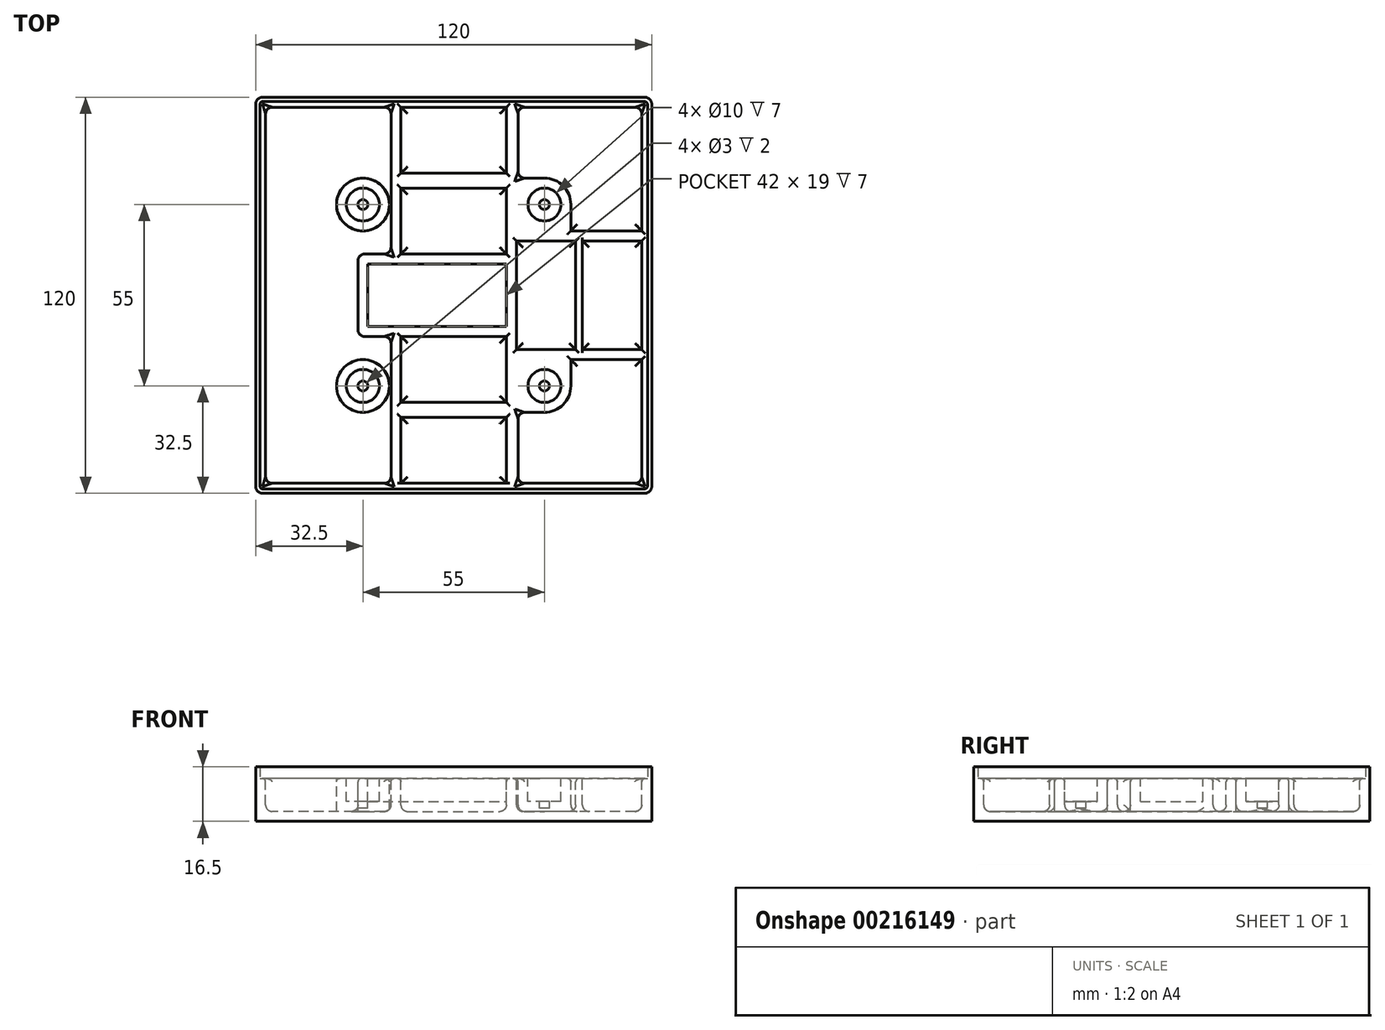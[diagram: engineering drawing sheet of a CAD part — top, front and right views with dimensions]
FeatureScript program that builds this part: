
annotation { "Feature Type Name" : "Feature", "Feature Type Description" : "" }
export const myFeature = defineFeature(function(context is Context, id is Id, definition is map)
    precondition{}
    {
        {
            var Q0;
            Q0=qCreatedBy(makeId("Top.planeOp"),FACE);
            var sketch = newSketch(context, id + "F0", { "sketchPlane" : qUnion([Q0])});
            skLineSegment(sketch, "E0.bottom", {"start": v(60, -60) * mm, "end": v(-60, -60) * mm});
            skLineSegment(sketch, "E0.top", {"start": v(60, 60) * mm, "end": v(-60, 60) * mm});
            skLineSegment(sketch, "E0.left", {"start": v(60, -60) * mm, "end": v(60, 60) * mm});
            skLineSegment(sketch, "E0.right", {"start": v(-60, -60) * mm, "end": v(-60, 60) * mm});
            skPoint(sketch, "E0.middle", {"position": v(0, 0) * mm});
            skSolve(sketch);
        }
        {
            var Q0;
            Q0=makeQuery(id+"F0.imprint","IMPRINT",FACE,{"disambiguationData":[TD([[makeQuery(id+"F0.imprint","IMPRINT",EDGE,{"derivedFrom":sQuery(id+"F0.wireOp",EDGE,"E0.bottom")}),-1.0]])]});
            extrude(context, id + "F1", {"entities" : qUnion([Q0]), "depth" : 13 * mm});
        }
        {
            var Q0;
            Q0=makeQuery(id+"F1.opExtrude","CAP_FACE",FACE,{"disambiguationData":[OSD([sQuery(id+"F0.wireOp",EDGE,"E0.bottom"),sQuery(id+"F0.wireOp",EDGE,"E0.top"),sQuery(id+"F0.wireOp",EDGE,"E0.left"),sQuery(id+"F0.wireOp",EDGE,"E0.right")])],"isStart":false});
            var sketch = newSketch(context, id + "F2", { "sketchPlane" : qUnion([Q0])});
            skLineSegment(sketch, "E1.bottom", {"start": v(16, -9.5) * mm, "end": v(-16, -9.5) * mm});
            skLineSegment(sketch, "E1.top", {"start": v(16, 9.5) * mm, "end": v(-16, 9.5) * mm});
            skLineSegment(sketch, "E1.left", {"start": v(16, -9.5) * mm, "end": v(16, 9.5) * mm});
            skLineSegment(sketch, "E1.right", {"start": v(-16, -9.5) * mm, "end": v(-16, 9.5) * mm});
            skPoint(sketch, "E1.middle", {"position": v(0, 0) * mm});
            skLineSegment(sketch, "E2", {"start": v(-16, 9.5) * mm, "end": v(-26, 9.5) * mm});
            skLineSegment(sketch, "E3", {"start": v(-26, 9.5) * mm, "end": v(-26, -9.5) * mm});
            skLineSegment(sketch, "E4", {"start": v(-26, -9.5) * mm, "end": v(-16, -9.5) * mm});
            skCircle(sketch, "E5", {"center": v(-27.5, 27.5) * mm, "radius": 5 * mm});
            skCircle(sketch, "E6", {"center": v(-27.5, -27.5) * mm, "radius": 5 * mm});
            skCircle(sketch, "E7", {"center": v(27.5, -27.5) * mm, "radius": 5 * mm});
            skCircle(sketch, "E8", {"center": v(27.5, 27.5) * mm, "radius": 5 * mm});
            skCircle(sketch, "E9", {"center": v(-27.5, 27.5) * mm, "radius": 1.5 * mm});
            skCircle(sketch, "E10", {"center": v(-27.5, -27.5) * mm, "radius": 1.5 * mm});
            skCircle(sketch, "E11", {"center": v(27.5, -27.5) * mm, "radius": 1.5 * mm});
            skCircle(sketch, "E12", {"center": v(27.5, 27.5) * mm, "radius": 1.5 * mm});
            skCircle(sketch, "E13.0", {"center": v(-27.5, 27.5) * mm, "radius": 8 * mm});
            skCircle(sketch, "E14.0", {"center": v(27.5, 27.5) * mm, "radius": 8 * mm});
            skCircle(sketch, "E15.0", {"center": v(27.5, -27.5) * mm, "radius": 8 * mm});
            skCircle(sketch, "E16.0", {"center": v(-27.5, -27.5) * mm, "radius": 8 * mm});
            skLineSegment(sketch, "E17.0", {"start": v(19, -12.5) * mm, "end": v(19, 12.5) * mm});
            skLineSegment(sketch, "E17.1", {"start": v(-29, -12.5) * mm, "end": v(-16, -12.5) * mm});
            skLineSegment(sketch, "E17.2", {"start": v(-29, 12.5) * mm, "end": v(-29, -12.5) * mm});
            skLineSegment(sketch, "E17.3", {"start": v(19, -12.5) * mm, "end": v(-16, -12.5) * mm});
            skLineSegment(sketch, "E17.4", {"start": v(-16, 12.5) * mm, "end": v(-29, 12.5) * mm});
            skLineSegment(sketch, "E17.5", {"start": v(19, 12.5) * mm, "end": v(-16, 12.5) * mm});
            skLineSegment(sketch, "E18.0", {"start": v(-57, -57) * mm, "end": v(-57, 57) * mm});
            skLineSegment(sketch, "E18.1", {"start": v(57, -57) * mm, "end": v(-57, -57) * mm});
            skLineSegment(sketch, "E18.2", {"start": v(57, -57) * mm, "end": v(57, 57) * mm});
            skLineSegment(sketch, "E18.3", {"start": v(57, 57) * mm, "end": v(-57, 57) * mm});
            skLineSegment(sketch, "E19", {"start": v(-16, 12.5) * mm, "end": v(-16, 57) * mm});
            skLineSegment(sketch, "E20", {"start": v(16, 12.5) * mm, "end": v(16, 57) * mm});
            skLineSegment(sketch, "E21", {"start": v(-16, 32.5) * mm, "end": v(16, 32.5) * mm});
            skLineSegment(sketch, "E22", {"start": v(19, 12.5) * mm, "end": v(19, 16.5) * mm});
            skLineSegment(sketch, "E23", {"start": v(19, 16.5) * mm, "end": v(37, 16.5) * mm});
            skLineSegment(sketch, "E24", {"start": v(37, 16.5) * mm, "end": v(37, -16.5) * mm});
            skLineSegment(sketch, "E25", {"start": v(37, -16.5) * mm, "end": v(19, -16.5) * mm});
            skLineSegment(sketch, "E26", {"start": v(19, -16.5) * mm, "end": v(19, -12.5) * mm});
            skLineSegment(sketch, "E27", {"start": v(-16, -12.5) * mm, "end": v(-16, -57) * mm});
            skLineSegment(sketch, "E28", {"start": v(16, -12.5) * mm, "end": v(16, -57) * mm});
            skLineSegment(sketch, "E29", {"start": v(-16, -32.5) * mm, "end": v(16, -32.5) * mm});
            skLineSegment(sketch, "E30", {"start": v(-19, 57) * mm, "end": v(-19, 12.5) * mm});
            skLineSegment(sketch, "E31", {"start": v(-19, -12.5) * mm, "end": v(-19, -57) * mm});
            skLineSegment(sketch, "E32", {"start": v(-16, -37) * mm, "end": v(16, -37) * mm});
            skLineSegment(sketch, "E33", {"start": v(-16, 37) * mm, "end": v(16, 37) * mm});
            skLineSegment(sketch, "E34", {"start": v(19.5, 57) * mm, "end": v(19.5, 27.5) * mm});
            skLineSegment(sketch, "E35", {"start": v(19.5, -57) * mm, "end": v(19.5, -27.5) * mm});
            skLineSegment(sketch, "E36", {"start": v(19.5, -35.5) * mm, "end": v(27.5, -35.5) * mm});
            skLineSegment(sketch, "E37", {"start": v(19.5, 35.5) * mm, "end": v(27.5, 35.5) * mm});
            skLineSegment(sketch, "E38", {"start": v(57, 19.5) * mm, "end": v(27.5, 19.5) * mm});
            skLineSegment(sketch, "E39", {"start": v(35.5, 19.5) * mm, "end": v(35.5, 27.5) * mm});
            skLineSegment(sketch, "E40", {"start": v(57, -19.5) * mm, "end": v(27.5, -19.5) * mm});
            skLineSegment(sketch, "E41", {"start": v(35.5, -19.5) * mm, "end": v(35.5, -27.5) * mm});
            skLineSegment(sketch, "E42", {"start": v(57, 16.5) * mm, "end": v(39, 16.5) * mm});
            skLineSegment(sketch, "E43", {"start": v(39, 16.5) * mm, "end": v(39, -16.5) * mm});
            skLineSegment(sketch, "E44", {"start": v(39, -16.5) * mm, "end": v(57, -16.5) * mm});
            skSolve(sketch);
        }
        {
            var Q0;
            Q0=makeQuery(id+"F2.imprint","IMPRINT",FACE,{"disambiguationData":[TD([[makeQuery(id+"F2.imprint","IMPRINT",EDGE,{"derivedFrom":sQuery(id+"F2.wireOp",EDGE,"E1.right")}),1.0]])]});
            var Q1;
            Q1=makeQuery(id+"F2.imprint","IMPRINT",FACE,{"disambiguationData":[TD([[makeQuery(id+"F2.imprint","IMPRINT",EDGE,{"derivedFrom":sQuery(id+"F2.wireOp",EDGE,"E1.bottom")}),-1.0]])]});
            extrude(context, id + "F3", {"entities" : qUnion([Q0, Q1]), "operationType" : NewBodyOperationType.REMOVE, "oppositeDirection" : true, "depth" : 7 * mm});
        }
        {
            var Q0;
            Q0=makeQuery(id+"F2.imprint","IMPRINT",FACE,{"disambiguationData":[TD([[makeQuery(id+"F2.imprint","IMPRINT",EDGE,{"derivedFrom":sQuery(id+"F2.wireOp",EDGE,"E5")}),1.0]])]});
            var Q1;
            Q1=makeQuery(id+"F2.imprint","IMPRINT",FACE,{"disambiguationData":[TD([[makeQuery(id+"F2.imprint","IMPRINT",EDGE,{"derivedFrom":sQuery(id+"F2.wireOp",EDGE,"E6")}),1.0]])]});
            var Q2;
            Q2=makeQuery(id+"F2.imprint","IMPRINT",FACE,{"disambiguationData":[TD([[makeQuery(id+"F2.imprint","IMPRINT",EDGE,{"derivedFrom":sQuery(id+"F2.wireOp",EDGE,"E7")}),1.0]])]});
            var Q3;
            Q3=makeQuery(id+"F2.imprint","IMPRINT",FACE,{"disambiguationData":[TD([[makeQuery(id+"F2.imprint","IMPRINT",EDGE,{"derivedFrom":sQuery(id+"F2.wireOp",EDGE,"E8")}),1.0]])]});
            extrude(context, id + "F4", {"entities" : qUnion([Q0, Q1, Q2, Q3]), "operationType" : NewBodyOperationType.REMOVE, "oppositeDirection" : true, "depth" : 7 * mm});
        }
        {
            var Q0;
            Q0=makeQuery(id+"F2.imprint","IMPRINT",FACE,{"disambiguationData":[TD([[makeQuery(id+"F2.imprint","IMPRINT",EDGE,{"derivedFrom":sQuery(id+"F2.wireOp",EDGE,"E9")}),1.0]])]});
            var Q1;
            Q1=makeQuery(id+"F2.imprint","IMPRINT",FACE,{"disambiguationData":[TD([[makeQuery(id+"F2.imprint","IMPRINT",EDGE,{"derivedFrom":sQuery(id+"F2.wireOp",EDGE,"E12")}),1.0]])]});
            var Q2;
            Q2=makeQuery(id+"F2.imprint","IMPRINT",FACE,{"disambiguationData":[TD([[makeQuery(id+"F2.imprint","IMPRINT",EDGE,{"derivedFrom":sQuery(id+"F2.wireOp",EDGE,"E11")}),1.0]])]});
            var Q3;
            Q3=makeQuery(id+"F2.imprint","IMPRINT",FACE,{"disambiguationData":[TD([[makeQuery(id+"F2.imprint","IMPRINT",EDGE,{"derivedFrom":sQuery(id+"F2.wireOp",EDGE,"E10")}),1.0]])]});
            extrude(context, id + "F5", {"entities" : qUnion([Q0, Q1, Q2, Q3]), "operationType" : NewBodyOperationType.REMOVE, "oppositeDirection" : true, "depth" : 9 * mm});
        }
        {
            var Q0;
            {var subQ5=sQuery(id+"F2.wireOp",EDGE,"FMWFYpV9-Ew7e-ZcVp-ZZrZ-oKRKmoRq2qlx");Q0=makeQuery(id+"F2.imprint","IMPRINT",FACE,{"disambiguationData":[TD([[makeQuery(id+"F2.imprint","IMPRINT",EDGE,{"derivedFrom":subQ5}),1.0]])]});}
            var Q1;
            {var subQ5=sQuery(id+"F2.wireOp",EDGE,"E21");Q1=makeQuery(id+"F2.imprint","IMPRINT",FACE,{"disambiguationData":[TD([[makeQuery(id+"F2.imprint","IMPRINT",EDGE,{"derivedFrom":subQ5}),-1.0]])]});}
            var Q2;
            Q2=makeQuery(id+"F2.imprint","IMPRINT",FACE,{"disambiguationData":[TD([[makeQuery(id+"F2.imprint","IMPRINT",EDGE,{"derivedFrom":sQuery(id+"F2.wireOp",EDGE,"E13.0")}),-1.0]])]});
            var Q3;
            {var subQ5=sQuery(id+"F2.wireOp",EDGE,"E29");Q3=makeQuery(id+"F2.imprint","IMPRINT",FACE,{"disambiguationData":[TD([[makeQuery(id+"F2.imprint","IMPRINT",EDGE,{"derivedFrom":subQ5}),1.0]])]});}
            var Q4;
            {var subQ5=sQuery(id+"F2.wireOp",EDGE,"E32");Q4=makeQuery(id+"F2.imprint","IMPRINT",FACE,{"disambiguationData":[TD([[makeQuery(id+"F2.imprint","IMPRINT",EDGE,{"derivedFrom":subQ5}),-1.0]])]});}
            var Q5;
            {var subQ3=sQuery(id+"F2.wireOp",EDGE,"E36");Q5=makeQuery(id+"F2.imprint","IMPRINT",FACE,{"disambiguationData":[TD([[makeQuery(id+"F2.imprint","IMPRINT",EDGE,{"derivedFrom":subQ3}),-1.0]])]});}
            var Q6;
            Q6=makeQuery(id+"F2.imprint","IMPRINT",FACE,{"disambiguationData":[TD([[makeQuery(id+"F2.imprint","IMPRINT",EDGE,{"derivedFrom":sQuery(id+"F2.wireOp",EDGE,"E17.0")}),-1.0]])]});
            var Q7;
            {var subQ0=sQuery(id+"F2.wireOp",EDGE,"E42");Q7=makeQuery(id+"F2.imprint","IMPRINT",FACE,{"disambiguationData":[TD([[makeQuery(id+"F2.imprint","IMPRINT",EDGE,{"derivedFrom":subQ0}),1.0]])]});}
            var Q8;
            {var subQ5=sQuery(id+"F2.wireOp",EDGE,"E37");Q8=makeQuery(id+"F2.imprint","IMPRINT",FACE,{"disambiguationData":[TD([[makeQuery(id+"F2.imprint","IMPRINT",EDGE,{"derivedFrom":subQ5}),1.0]])]});}
            var Q9;
            {var subQ5=sQuery(id+"F2.wireOp",EDGE,"E33");Q9=makeQuery(id+"F2.imprint","IMPRINT",FACE,{"disambiguationData":[TD([[makeQuery(id+"F2.imprint","IMPRINT",EDGE,{"derivedFrom":subQ5}),1.0]])]});}
            extrude(context, id + "F6", {"entities" : qUnion([Q0, Q1, Q2, Q3, Q4, Q5, Q6, Q7, Q8, Q9]), "operationType" : NewBodyOperationType.REMOVE, "oppositeDirection" : true, "depth" : 10 * mm});
        }
        {
            var Q0;
            {var subQ6=sQuery(id+"F2.wireOp",EDGE,"E18.0");Q0=makeQuery(id+"F2.imprint","IMPRINT",FACE,{"disambiguationData":[TD([[makeQuery(id+"F2.imprint","IMPRINT",EDGE,{"derivedFrom":subQ6}),1.0]])]});}
            var sketch = newSketch(context, id + "F7", { "sketchPlane" : qUnion([Q0])});
            skLineSegment(sketch, "E45.0", {"start": v(58.75, 58.75) * mm, "end": v(-58.75, 58.75) * mm});
            skLineSegment(sketch, "E45.1", {"start": v(58.75, -58.75) * mm, "end": v(58.75, 58.75) * mm});
            skLineSegment(sketch, "E45.2", {"start": v(58.75, -58.75) * mm, "end": v(-58.75, -58.75) * mm});
            skLineSegment(sketch, "E45.3", {"start": v(-58.75, -58.75) * mm, "end": v(-58.75, 58.75) * mm});
            skSolve(sketch);
        }
        {
            var Q0;
            Q0=makeQuery(id+"F7.imprint","IMPRINT",FACE,{"disambiguationData":[TD([[makeQuery(id+"F7.imprint","IMPRINT",EDGE,{"derivedFrom":sQuery(id+"F7.wireOp",EDGE,"E45.0")}),-1.0]])]});
            extrude(context, id + "F8", {"entities" : qUnion([Q0]), "operationType" : NewBodyOperationType.ADD, "depth" : 3.5 * mm});
        }
        {
            var Q0;
            Q0=makeQuery(id+"F4.boolean.opBoolean","COPY",EDGE,{"derivedFrom":makeQuery(id+"F4.opExtrude","CAP_EDGE",EDGE,{"disambiguationData":[OSD([sQuery(id+"F2.wireOp",EDGE,"E5")])],"isStart":true})});
            var Q1;
            Q1=makeQuery(id+"F4.boolean.opBoolean","COPY",EDGE,{"derivedFrom":makeQuery(id+"F4.opExtrude","CAP_EDGE",EDGE,{"disambiguationData":[OSD([sQuery(id+"F2.wireOp",EDGE,"E8")])],"isStart":true})});
            var Q2;
            Q2=makeQuery(id+"F3.boolean.opBoolean","COPY",EDGE,{"derivedFrom":makeQuery(id+"F3.opExtrude","CAP_EDGE",EDGE,{"disambiguationData":[OSD([sQuery(id+"F2.wireOp",EDGE,"E1.top"),sQuery(id+"F2.wireOp",EDGE,"E2")])],"isStart":true})});
            var Q3;
            Q3=makeQuery(id+"F3.boolean.opBoolean","COPY",EDGE,{"derivedFrom":makeQuery(id+"F3.opExtrude","CAP_EDGE",EDGE,{"disambiguationData":[OSD([sQuery(id+"F2.wireOp",EDGE,"E1.left")])],"isStart":true})});
            var Q4;
            Q4=makeQuery(id+"F3.boolean.opBoolean","COPY",EDGE,{"derivedFrom":makeQuery(id+"F3.opExtrude","CAP_EDGE",EDGE,{"disambiguationData":[OSD([sQuery(id+"F2.wireOp",EDGE,"E1.bottom"),sQuery(id+"F2.wireOp",EDGE,"E4")])],"isStart":true})});
            var Q5;
            Q5=makeQuery(id+"F3.boolean.opBoolean","COPY",EDGE,{"derivedFrom":makeQuery(id+"F3.opExtrude","CAP_EDGE",EDGE,{"disambiguationData":[OSD([sQuery(id+"F2.wireOp",EDGE,"E3")])],"isStart":true})});
            var Q6;
            Q6=makeQuery(id+"F4.boolean.opBoolean","COPY",EDGE,{"derivedFrom":makeQuery(id+"F4.opExtrude","CAP_EDGE",EDGE,{"disambiguationData":[OSD([sQuery(id+"F2.wireOp",EDGE,"E6")])],"isStart":true})});
            var Q7;
            Q7=makeQuery(id+"F4.boolean.opBoolean","COPY",EDGE,{"derivedFrom":makeQuery(id+"F4.opExtrude","CAP_EDGE",EDGE,{"disambiguationData":[OSD([sQuery(id+"F2.wireOp",EDGE,"E7")])],"isStart":true})});
            var Q8;
            {var subQ0=sQuery(id+"F2.wireOp",EDGE,"E19");Q8=makeQuery(id+"F6.boolean.opBoolean","COPY",EDGE,{"derivedFrom":makeQuery(id+"F6.opExtrude","CAP_EDGE",EDGE,{"disambiguationData":[OSD([subQ0]),TDD([makeQuery(id+"F2.imprint","IMPRINT",EDGE,{"disambiguationData":[TD([[makeQuery(id+"F2.imprint","INTERSECT",VERTEX,{"derivedFrom":[subQ0,sQuery(id+"F2.wireOp",EDGE,"E21")]}),1.0]])],"derivedFrom":subQ0})])],"isStart":true})});}
            var Q9;
            Q9=makeQuery(id+"F6.boolean.opBoolean","COPY",EDGE,{"derivedFrom":makeQuery(id+"F6.opExtrude","CAP_EDGE",EDGE,{"disambiguationData":[OSD([sQuery(id+"F2.wireOp",EDGE,"E17.5")])],"isStart":true})});
            var Q10;
            Q10=makeQuery(id+"F6.boolean.opBoolean","COPY",EDGE,{"derivedFrom":makeQuery(id+"F6.opExtrude","CAP_EDGE",EDGE,{"disambiguationData":[OSD([sQuery(id+"F2.wireOp",EDGE,"E21")])],"isStart":true})});
            var Q11;
            {var subQ0=sQuery(id+"F2.wireOp",EDGE,"E19");Q11=makeQuery(id+"F6.boolean.opBoolean","COPY",EDGE,{"derivedFrom":makeQuery(id+"F6.opExtrude","CAP_EDGE",EDGE,{"disambiguationData":[OSD([subQ0]),TDD([makeQuery(id+"F2.imprint","IMPRINT",EDGE,{"disambiguationData":[TD([[makeQuery(id+"F2.imprint","INTERSECT",VERTEX,{"derivedFrom":[sQuery(id+"F2.wireOp",EDGE,"E18.3"),subQ0]}),1.0]])],"derivedFrom":subQ0})])],"isStart":true})});}
            var Q12;
            Q12=makeQuery(id+"F6.boolean.opBoolean","COPY",EDGE,{"derivedFrom":makeQuery(id+"F6.opExtrude","CAP_EDGE",EDGE,{"disambiguationData":[OSD([sQuery(id+"F2.wireOp",EDGE,"FMWFYpV9-Ew7e-ZcVp-ZZrZ-oKRKmoRq2qlx")])],"isStart":true})});
            var Q13;
            {var subQ0=sQuery(id+"F2.wireOp",EDGE,"E20");Q13=makeQuery(id+"F6.boolean.opBoolean","COPY",EDGE,{"derivedFrom":makeQuery(id+"F6.opExtrude","CAP_EDGE",EDGE,{"disambiguationData":[OSD([subQ0]),TDD([makeQuery(id+"F2.imprint","IMPRINT",EDGE,{"disambiguationData":[TD([[makeQuery(id+"F2.imprint","INTERSECT",VERTEX,{"derivedFrom":[sQuery(id+"F2.wireOp",EDGE,"E18.3"),subQ0]}),1.0]])],"derivedFrom":subQ0})])],"isStart":true})});}
            var Q14;
            Q14=makeQuery(id+"F6.boolean.opBoolean","COPY",EDGE,{"derivedFrom":makeQuery(id+"F6.opExtrude","CAP_EDGE",EDGE,{"disambiguationData":[OSD([sQuery(id+"F2.wireOp",EDGE,"E17.0"),sQuery(id+"F2.wireOp",EDGE,"E22"),sQuery(id+"F2.wireOp",EDGE,"E26")])],"isStart":true})});
            var Q15;
            Q15=makeQuery(id+"F6.boolean.opBoolean","COPY",EDGE,{"derivedFrom":makeQuery(id+"F6.opExtrude","CAP_EDGE",EDGE,{"disambiguationData":[OSD([sQuery(id+"F2.wireOp",EDGE,"E23")])],"isStart":true})});
            var Q16;
            Q16=makeQuery(id+"F6.boolean.opBoolean","COPY",EDGE,{"derivedFrom":makeQuery(id+"F6.opExtrude","CAP_EDGE",EDGE,{"disambiguationData":[OSD([sQuery(id+"F2.wireOp",EDGE,"E24")])],"isStart":true})});
            var Q17;
            Q17=makeQuery(id+"F6.boolean.opBoolean","COPY",EDGE,{"derivedFrom":makeQuery(id+"F6.opExtrude","CAP_EDGE",EDGE,{"disambiguationData":[OSD([sQuery(id+"F2.wireOp",EDGE,"E25")])],"isStart":true})});
            var Q18;
            {var subQ0=sQuery(id+"F2.wireOp",EDGE,"E28");Q18=makeQuery(id+"F6.boolean.opBoolean","COPY",EDGE,{"derivedFrom":makeQuery(id+"F6.opExtrude","CAP_EDGE",EDGE,{"disambiguationData":[OSD([subQ0]),TDD([makeQuery(id+"F2.imprint","IMPRINT",EDGE,{"disambiguationData":[TD([[makeQuery(id+"F2.imprint","INTERSECT",VERTEX,{"derivedFrom":[sQuery(id+"F2.wireOp",EDGE,"E17.3"),subQ0]}),-1.0]])],"derivedFrom":subQ0})])],"isStart":true})});}
            var Q19;
            {var subQ0=sQuery(id+"F2.wireOp",EDGE,"E28");Q19=makeQuery(id+"F6.boolean.opBoolean","COPY",EDGE,{"derivedFrom":makeQuery(id+"F6.opExtrude","CAP_EDGE",EDGE,{"disambiguationData":[OSD([subQ0]),TDD([makeQuery(id+"F2.imprint","IMPRINT",EDGE,{"disambiguationData":[TD([[makeQuery(id+"F2.imprint","INTERSECT",VERTEX,{"derivedFrom":[sQuery(id+"F2.wireOp",EDGE,"E18.1"),subQ0]}),1.0]])],"derivedFrom":subQ0})])],"isStart":true})});}
            var Q20;
            Q20=makeQuery(id+"F6.boolean.opBoolean","COPY",EDGE,{"derivedFrom":makeQuery(id+"F6.opExtrude","CAP_EDGE",EDGE,{"disambiguationData":[OSD([sQuery(id+"F2.wireOp",EDGE,"KB4tX4Ro-G294-vaRV-RxTP-gQnuyON8fFV4")])],"isStart":true})});
            var Q21;
            Q21=makeQuery(id+"F6.boolean.opBoolean","COPY",EDGE,{"derivedFrom":makeQuery(id+"F6.opExtrude","CAP_EDGE",EDGE,{"disambiguationData":[OSD([sQuery(id+"F2.wireOp",EDGE,"E29")])],"isStart":true})});
            var Q22;
            Q22=makeQuery(id+"F6.boolean.opBoolean","COPY",EDGE,{"derivedFrom":makeQuery(id+"F6.opExtrude","CAP_EDGE",EDGE,{"disambiguationData":[OSD([sQuery(id+"F2.wireOp",EDGE,"E17.3")])],"isStart":true})});
            var Q23;
            {var subQ0=sQuery(id+"F2.wireOp",EDGE,"E27");Q23=makeQuery(id+"F6.boolean.opBoolean","COPY",EDGE,{"derivedFrom":makeQuery(id+"F6.opExtrude","CAP_EDGE",EDGE,{"disambiguationData":[OSD([subQ0]),TDD([makeQuery(id+"F2.imprint","IMPRINT",EDGE,{"disambiguationData":[TD([[makeQuery(id+"F2.imprint","INTERSECT",VERTEX,{"derivedFrom":[subQ0,sQuery(id+"F2.wireOp",EDGE,"E29")]}),1.0]])],"derivedFrom":subQ0})])],"isStart":true})});}
            var Q24;
            {var subQ0=sQuery(id+"F2.wireOp",EDGE,"E27");Q24=makeQuery(id+"F6.boolean.opBoolean","COPY",EDGE,{"derivedFrom":makeQuery(id+"F6.opExtrude","CAP_EDGE",EDGE,{"disambiguationData":[OSD([subQ0]),TDD([makeQuery(id+"F2.imprint","IMPRINT",EDGE,{"disambiguationData":[TD([[makeQuery(id+"F2.imprint","INTERSECT",VERTEX,{"derivedFrom":[sQuery(id+"F2.wireOp",EDGE,"E18.1"),subQ0]}),1.0]])],"derivedFrom":subQ0})])],"isStart":true})});}
            var Q25;
            {var subQ0=sQuery(id+"F2.wireOp",EDGE,"E20");Q25=makeQuery(id+"F6.boolean.opBoolean","COPY",EDGE,{"derivedFrom":makeQuery(id+"F6.opExtrude","CAP_EDGE",EDGE,{"disambiguationData":[OSD([subQ0]),TDD([makeQuery(id+"F2.imprint","IMPRINT",EDGE,{"disambiguationData":[TD([[makeQuery(id+"F2.imprint","INTERSECT",VERTEX,{"derivedFrom":[sQuery(id+"F2.wireOp",EDGE,"E17.5"),subQ0]}),-1.0]])],"derivedFrom":subQ0})])],"isStart":true})});}
            var Q26;
            Q26=makeQuery(id+"F6.boolean.opBoolean","COPY",EDGE,{"derivedFrom":makeQuery(id+"F6.opExtrude","CAP_EDGE",EDGE,{"disambiguationData":[OSD([sQuery(id+"F2.wireOp",EDGE,"E16.0")])],"isStart":true})});
            var Q27;
            Q27=makeQuery(id+"F6.boolean.opBoolean","COPY",EDGE,{"derivedFrom":makeQuery(id+"F6.opExtrude","CAP_EDGE",EDGE,{"disambiguationData":[OSD([sQuery(id+"F2.wireOp",EDGE,"E13.0")])],"isStart":true})});
            var Q28;
            {var subQ0=sQuery(id+"F2.wireOp",EDGE,"E19");Q28=makeQuery(id+"F6.boolean.opBoolean","COPY",EDGE,{"derivedFrom":makeQuery(id+"F6.opExtrude","CAP_EDGE",EDGE,{"disambiguationData":[OSD([subQ0]),TDD([makeQuery(id+"F2.imprint","IMPRINT",EDGE,{"disambiguationData":[TD([[makeQuery(id+"F2.imprint","INTERSECT",VERTEX,{"derivedFrom":[subQ0,sQuery(id+"F2.wireOp",EDGE,"72itZujO-k5kq-emlP-LSjC-fSTvy6e93rC8")]}),1.0]])],"derivedFrom":subQ0})])],"isStart":true})});}
            var Q29;
            Q29=makeQuery(id+"F6.boolean.opBoolean","COPY",EDGE,{"derivedFrom":makeQuery(id+"F6.opExtrude","CAP_EDGE",EDGE,{"disambiguationData":[OSD([sQuery(id+"F2.wireOp",EDGE,"72itZujO-k5kq-emlP-LSjC-fSTvy6e93rC8")])],"isStart":true})});
            var Q30;
            Q30=makeQuery(id+"F6.boolean.opBoolean","COPY",EDGE,{"derivedFrom":makeQuery(id+"F6.opExtrude","CAP_EDGE",EDGE,{"disambiguationData":[OSD([sQuery(id+"F2.wireOp",EDGE,"E33")])],"isStart":true})});
            var Q31;
            {var subQ0=sQuery(id+"F2.wireOp",EDGE,"E20");Q31=makeQuery(id+"F6.boolean.opBoolean","COPY",EDGE,{"derivedFrom":makeQuery(id+"F6.opExtrude","CAP_EDGE",EDGE,{"disambiguationData":[OSD([subQ0]),TDD([makeQuery(id+"F2.imprint","IMPRINT",EDGE,{"disambiguationData":[TD([[makeQuery(id+"F2.imprint","INTERSECT",VERTEX,{"derivedFrom":[subQ0,sQuery(id+"F2.wireOp",EDGE,"72itZujO-k5kq-emlP-LSjC-fSTvy6e93rC8")]}),1.0]])],"derivedFrom":subQ0})])],"isStart":true})});}
            var Q32;
            Q32=makeQuery(id+"F6.boolean.opBoolean","COPY",EDGE,{"derivedFrom":makeQuery(id+"F6.opExtrude","CAP_EDGE",EDGE,{"disambiguationData":[OSD([sQuery(id+"F2.wireOp",EDGE,"E32")])],"isStart":true})});
            var Q33;
            {var subQ0=sQuery(id+"F2.wireOp",EDGE,"E27");Q33=makeQuery(id+"F6.boolean.opBoolean","COPY",EDGE,{"derivedFrom":makeQuery(id+"F6.opExtrude","CAP_EDGE",EDGE,{"disambiguationData":[OSD([subQ0]),TDD([makeQuery(id+"F2.imprint","IMPRINT",EDGE,{"disambiguationData":[TD([[makeQuery(id+"F2.imprint","INTERSECT",VERTEX,{"derivedFrom":[subQ0,sQuery(id+"F2.wireOp",EDGE,"E32")]}),-1.0]])],"derivedFrom":subQ0})])],"isStart":true})});}
            var Q34;
            Q34=makeQuery(id+"F6.boolean.opBoolean","COPY",EDGE,{"derivedFrom":makeQuery(id+"F6.opExtrude","CAP_EDGE",EDGE,{"disambiguationData":[OSD([sQuery(id+"F2.wireOp",EDGE,"oXTIdJ37-I2Sm-Fy2X-7b5Y-V1gPf1k4f7kg")])],"isStart":true})});
            var Q35;
            {var subQ0=sQuery(id+"F2.wireOp",EDGE,"E28");Q35=makeQuery(id+"F6.boolean.opBoolean","COPY",EDGE,{"derivedFrom":makeQuery(id+"F6.opExtrude","CAP_EDGE",EDGE,{"disambiguationData":[OSD([subQ0]),TDD([makeQuery(id+"F2.imprint","IMPRINT",EDGE,{"disambiguationData":[TD([[makeQuery(id+"F2.imprint","INTERSECT",VERTEX,{"derivedFrom":[subQ0,sQuery(id+"F2.wireOp",EDGE,"E32")]}),-1.0]])],"derivedFrom":subQ0})])],"isStart":true})});}
            var Q36;
            {var subQ0=sQuery(id+"F2.wireOp",EDGE,"E18.3");Q36=makeQuery(id+"F6.boolean.opBoolean","COPY",EDGE,{"derivedFrom":makeQuery(id+"F6.opExtrude","CAP_EDGE",EDGE,{"disambiguationData":[OSD([subQ0]),TDD([makeQuery(id+"F2.imprint","IMPRINT",EDGE,{"disambiguationData":[TD([[makeQuery(id+"F2.imprint","INTERSECT",VERTEX,{"derivedFrom":[subQ0,sQuery(id+"F2.wireOp",EDGE,"E19")]}),1.0]])],"derivedFrom":subQ0})])],"isStart":true})});}
            var Q37;
            Q37=makeQuery(id+"F6.boolean.opBoolean","COPY",EDGE,{"derivedFrom":makeQuery(id+"F6.opExtrude","CAP_EDGE",EDGE,{"disambiguationData":[OSD([sQuery(id+"F2.wireOp",EDGE,"E42")])],"isStart":true})});
            var Q38;
            {var subQ0=sQuery(id+"F2.wireOp",EDGE,"E18.2");Q38=makeQuery(id+"F6.boolean.opBoolean","COPY",EDGE,{"derivedFrom":makeQuery(id+"F6.opExtrude","CAP_EDGE",EDGE,{"disambiguationData":[OSD([subQ0]),TDD([makeQuery(id+"F2.imprint","IMPRINT",EDGE,{"disambiguationData":[TD([[makeQuery(id+"F2.imprint","INTERSECT",VERTEX,{"derivedFrom":[subQ0,sQuery(id+"F2.wireOp",EDGE,"E42")]}),1.0]])],"derivedFrom":subQ0})])],"isStart":true})});}
            var Q39;
            Q39=makeQuery(id+"F6.boolean.opBoolean","COPY",EDGE,{"derivedFrom":makeQuery(id+"F6.opExtrude","CAP_EDGE",EDGE,{"disambiguationData":[OSD([sQuery(id+"F2.wireOp",EDGE,"E44")])],"isStart":true})});
            var Q40;
            {var subQ0=sQuery(id+"F2.wireOp",EDGE,"E18.2");Q40=makeQuery(id+"F6.boolean.opBoolean","COPY",EDGE,{"derivedFrom":makeQuery(id+"F6.opExtrude","CAP_EDGE",EDGE,{"disambiguationData":[OSD([subQ0]),TDD([makeQuery(id+"F2.imprint","IMPRINT",EDGE,{"disambiguationData":[TD([[makeQuery(id+"F2.imprint","INTERSECT",VERTEX,{"derivedFrom":[sQuery(id+"F2.wireOp",EDGE,"E18.1"),subQ0]}),-1.0]])],"derivedFrom":subQ0})])],"isStart":true})});}
            var Q41;
            Q41=makeQuery(id+"F6.boolean.opBoolean","COPY",EDGE,{"derivedFrom":makeQuery(id+"F6.opExtrude","CAP_EDGE",EDGE,{"disambiguationData":[OSD([sQuery(id+"F2.wireOp",EDGE,"E40")])],"isStart":true})});
            var Q42;
            Q42=makeQuery(id+"F6.boolean.opBoolean","COPY",EDGE,{"derivedFrom":makeQuery(id+"F6.opExtrude","CAP_EDGE",EDGE,{"disambiguationData":[OSD([sQuery(id+"F2.wireOp",EDGE,"E15.0")])],"isStart":true})});
            var Q43;
            Q43=makeQuery(id+"F6.boolean.opBoolean","COPY",EDGE,{"derivedFrom":makeQuery(id+"F6.opExtrude","CAP_EDGE",EDGE,{"disambiguationData":[OSD([sQuery(id+"F2.wireOp",EDGE,"E35")])],"isStart":true})});
            var Q44;
            {var subQ0=sQuery(id+"F2.wireOp",EDGE,"E18.1");Q44=makeQuery(id+"F6.boolean.opBoolean","COPY",EDGE,{"derivedFrom":makeQuery(id+"F6.opExtrude","CAP_EDGE",EDGE,{"disambiguationData":[OSD([subQ0]),TDD([makeQuery(id+"F2.imprint","IMPRINT",EDGE,{"disambiguationData":[TD([[makeQuery(id+"F2.imprint","INTERSECT",VERTEX,{"derivedFrom":[subQ0,sQuery(id+"F2.wireOp",EDGE,"E18.2")]}),-1.0]])],"derivedFrom":subQ0})])],"isStart":true})});}
            var Q45;
            {var subQ0=sQuery(id+"F2.wireOp",EDGE,"E18.2");Q45=makeQuery(id+"F6.boolean.opBoolean","COPY",EDGE,{"derivedFrom":makeQuery(id+"F6.opExtrude","CAP_EDGE",EDGE,{"disambiguationData":[OSD([subQ0]),TDD([makeQuery(id+"F2.imprint","IMPRINT",EDGE,{"disambiguationData":[TD([[makeQuery(id+"F2.imprint","INTERSECT",VERTEX,{"derivedFrom":[subQ0,sQuery(id+"F2.wireOp",EDGE,"E18.3")]}),1.0]])],"derivedFrom":subQ0})])],"isStart":true})});}
            var Q46;
            {var subQ0=sQuery(id+"F2.wireOp",EDGE,"E18.3");Q46=makeQuery(id+"F6.boolean.opBoolean","COPY",EDGE,{"derivedFrom":makeQuery(id+"F6.opExtrude","CAP_EDGE",EDGE,{"disambiguationData":[OSD([subQ0]),TDD([makeQuery(id+"F2.imprint","IMPRINT",EDGE,{"disambiguationData":[TD([[makeQuery(id+"F2.imprint","INTERSECT",VERTEX,{"derivedFrom":[sQuery(id+"F2.wireOp",EDGE,"E18.2"),subQ0]}),-1.0]])],"derivedFrom":subQ0})])],"isStart":true})});}
            var Q47;
            Q47=makeQuery(id+"F6.boolean.opBoolean","COPY",EDGE,{"derivedFrom":makeQuery(id+"F6.opExtrude","CAP_EDGE",EDGE,{"disambiguationData":[OSD([sQuery(id+"F2.wireOp",EDGE,"E34")])],"isStart":true})});
            var Q48;
            Q48=makeQuery(id+"F6.boolean.opBoolean","COPY",EDGE,{"derivedFrom":makeQuery(id+"F6.opExtrude","CAP_EDGE",EDGE,{"disambiguationData":[OSD([sQuery(id+"F2.wireOp",EDGE,"E14.0")])],"isStart":true})});
            var Q49;
            Q49=makeQuery(id+"F6.boolean.opBoolean","COPY",EDGE,{"derivedFrom":makeQuery(id+"F6.opExtrude","CAP_EDGE",EDGE,{"disambiguationData":[OSD([sQuery(id+"F2.wireOp",EDGE,"E38")])],"isStart":true})});
            var Q50;
            Q50=makeQuery(id+"F6.boolean.opBoolean","COPY",EDGE,{"derivedFrom":makeQuery(id+"F6.opExtrude","CAP_EDGE",EDGE,{"disambiguationData":[OSD([sQuery(id+"F2.wireOp",EDGE,"E17.2")])],"isStart":true})});
            var Q51;
            Q51=makeQuery(id+"F6.boolean.opBoolean","COPY",EDGE,{"derivedFrom":makeQuery(id+"F6.opExtrude","CAP_EDGE",EDGE,{"disambiguationData":[OSD([sQuery(id+"F2.wireOp",EDGE,"E31")])],"isStart":true})});
            var Q52;
            Q52=makeQuery(id+"F6.boolean.opBoolean","COPY",EDGE,{"derivedFrom":makeQuery(id+"F6.opExtrude","CAP_EDGE",EDGE,{"disambiguationData":[OSD([sQuery(id+"F2.wireOp",EDGE,"E17.1")])],"isStart":true})});
            var Q53;
            Q53=makeQuery(id+"F6.boolean.opBoolean","COPY",EDGE,{"derivedFrom":makeQuery(id+"F6.opExtrude","CAP_EDGE",EDGE,{"disambiguationData":[OSD([sQuery(id+"F2.wireOp",EDGE,"E30")])],"isStart":true})});
            var Q54;
            Q54=makeQuery(id+"F6.boolean.opBoolean","COPY",EDGE,{"derivedFrom":makeQuery(id+"F6.opExtrude","CAP_EDGE",EDGE,{"disambiguationData":[OSD([sQuery(id+"F2.wireOp",EDGE,"E17.4")])],"isStart":true})});
            var Q55;
            Q55=makeQuery(id+"F6.boolean.opBoolean","COPY",EDGE,{"derivedFrom":makeQuery(id+"F6.opExtrude","CAP_EDGE",EDGE,{"disambiguationData":[OSD([sQuery(id+"F2.wireOp",EDGE,"E18.0")])],"isStart":true})});
            var Q56;
            {var subQ0=sQuery(id+"F2.wireOp",EDGE,"E18.1");Q56=makeQuery(id+"F6.boolean.opBoolean","COPY",EDGE,{"derivedFrom":makeQuery(id+"F6.opExtrude","CAP_EDGE",EDGE,{"disambiguationData":[OSD([subQ0]),TDD([makeQuery(id+"F2.imprint","IMPRINT",EDGE,{"disambiguationData":[TD([[makeQuery(id+"F2.imprint","INTERSECT",VERTEX,{"derivedFrom":[sQuery(id+"F2.wireOp",EDGE,"E18.0"),subQ0]}),1.0]])],"derivedFrom":subQ0})])],"isStart":true})});}
            var Q57;
            {var subQ0=sQuery(id+"F2.wireOp",EDGE,"E18.3");Q57=makeQuery(id+"F6.boolean.opBoolean","COPY",EDGE,{"derivedFrom":makeQuery(id+"F6.opExtrude","CAP_EDGE",EDGE,{"disambiguationData":[OSD([subQ0]),TDD([makeQuery(id+"F2.imprint","IMPRINT",EDGE,{"disambiguationData":[TD([[makeQuery(id+"F2.imprint","INTERSECT",VERTEX,{"derivedFrom":[sQuery(id+"F2.wireOp",EDGE,"E18.0"),subQ0]}),1.0]])],"derivedFrom":subQ0})])],"isStart":true})});}
            fillet(context, id + "F9", {"entities" : qUnion([Q0, Q1, Q2, Q3, Q4, Q5, Q6, Q7, Q8, Q9, Q10, Q11, Q12, Q13, Q14, Q15, Q16, Q17, Q18, Q19, Q20, Q21, Q22, Q23, Q24, Q25, Q26, Q27, Q28, Q29, Q30, Q31, Q32, Q33, Q34, Q35, Q36, Q37, Q38, Q39, Q40, Q41, Q42, Q43, Q44, Q45, Q46, Q47, Q48, Q49, Q50, Q51, Q52, Q53, Q54, Q55, Q56, Q57]), "radius" : 1 * mm, "tangentPropagation" : true, "allowEdgeOverflow" : false});
        }
        {
            var Q0;
            {var subQ0=sQuery(id+"F0.wireOp",EDGE,"E0.right");var subQ1=sQuery(id+"F0.wireOp",EDGE,"E0.bottom");Q0=makeQuery(id+"F8.boolean.opBoolean","MERGE",EDGE,{"derivedFrom":[makeQuery(id+"F1.opExtrude","SWEPT_EDGE",EDGE,{"disambiguationData":[OSD([subQ1,subQ0])]}),makeQuery(id+"F8.opExtrude","SWEPT_EDGE",EDGE,{"disambiguationData":[OSD([subQ1,subQ0])]})]});}
            var Q1;
            {var subQ0=sQuery(id+"F0.wireOp",EDGE,"E0.right");var subQ1=sQuery(id+"F0.wireOp",EDGE,"E0.top");Q1=makeQuery(id+"F8.boolean.opBoolean","MERGE",EDGE,{"derivedFrom":[makeQuery(id+"F1.opExtrude","SWEPT_EDGE",EDGE,{"disambiguationData":[OSD([subQ1,subQ0])]}),makeQuery(id+"F8.opExtrude","SWEPT_EDGE",EDGE,{"disambiguationData":[OSD([subQ1,subQ0])]})]});}
            var Q2;
            {var subQ0=sQuery(id+"F0.wireOp",EDGE,"E0.left");var subQ1=sQuery(id+"F0.wireOp",EDGE,"E0.top");Q2=makeQuery(id+"F8.boolean.opBoolean","MERGE",EDGE,{"derivedFrom":[makeQuery(id+"F1.opExtrude","SWEPT_EDGE",EDGE,{"disambiguationData":[OSD([subQ1,subQ0])]}),makeQuery(id+"F8.opExtrude","SWEPT_EDGE",EDGE,{"disambiguationData":[OSD([subQ1,subQ0])]})]});}
            var Q3;
            {var subQ0=sQuery(id+"F0.wireOp",EDGE,"E0.left");var subQ1=sQuery(id+"F0.wireOp",EDGE,"E0.bottom");Q3=makeQuery(id+"F8.boolean.opBoolean","MERGE",EDGE,{"derivedFrom":[makeQuery(id+"F1.opExtrude","SWEPT_EDGE",EDGE,{"disambiguationData":[OSD([subQ1,subQ0])]}),makeQuery(id+"F8.opExtrude","SWEPT_EDGE",EDGE,{"disambiguationData":[OSD([subQ1,subQ0])]})]});}
            var Q4;
            Q4=makeQuery(id+"F6.boolean.opBoolean","COPY",EDGE,{"derivedFrom":makeQuery(id+"F6.opExtrude","SWEPT_EDGE",EDGE,{"disambiguationData":[OSD([sQuery(id+"F2.wireOp",EDGE,"E18.0"),sQuery(id+"F2.wireOp",EDGE,"E18.3")])]})});
            var Q5;
            Q5=makeQuery(id+"F6.boolean.opBoolean","COPY",EDGE,{"derivedFrom":makeQuery(id+"F6.opExtrude","SWEPT_EDGE",EDGE,{"disambiguationData":[OSD([sQuery(id+"F2.wireOp",EDGE,"E18.0"),sQuery(id+"F2.wireOp",EDGE,"E18.1")])]})});
            var Q6;
            Q6=makeQuery(id+"F6.boolean.opBoolean","COPY",EDGE,{"derivedFrom":makeQuery(id+"F6.opExtrude","SWEPT_EDGE",EDGE,{"disambiguationData":[OSD([sQuery(id+"F2.wireOp",EDGE,"E18.1"),sQuery(id+"F2.wireOp",EDGE,"E18.2")])]})});
            var Q7;
            Q7=makeQuery(id+"F6.boolean.opBoolean","COPY",EDGE,{"derivedFrom":makeQuery(id+"F6.opExtrude","SWEPT_EDGE",EDGE,{"disambiguationData":[OSD([sQuery(id+"F2.wireOp",EDGE,"E18.2"),sQuery(id+"F2.wireOp",EDGE,"E18.3")])]})});
            var Q8;
            Q8=makeQuery(id+"F6.boolean.opBoolean","COPY",EDGE,{"derivedFrom":makeQuery(id+"F6.opExtrude","SWEPT_EDGE",EDGE,{"disambiguationData":[OSD([sQuery(id+"F2.wireOp",EDGE,"E18.3"),sQuery(id+"F2.wireOp",EDGE,"E34")])]})});
            var Q9;
            Q9=makeQuery(id+"F6.boolean.opBoolean","COPY",EDGE,{"derivedFrom":makeQuery(id+"F6.opExtrude","SWEPT_EDGE",EDGE,{"disambiguationData":[OSD([sQuery(id+"F2.wireOp",EDGE,"E35"),sQuery(id+"F2.wireOp",EDGE,"E36")])]})});
            var Q10;
            Q10=makeQuery(id+"F6.boolean.opBoolean","COPY",EDGE,{"derivedFrom":makeQuery(id+"F6.opExtrude","SWEPT_EDGE",EDGE,{"disambiguationData":[OSD([sQuery(id+"F2.wireOp",EDGE,"E34"),sQuery(id+"F2.wireOp",EDGE,"E37")])]})});
            var Q11;
            Q11=makeQuery(id+"F6.boolean.opBoolean","COPY",EDGE,{"derivedFrom":makeQuery(id+"F6.opExtrude","SWEPT_EDGE",EDGE,{"disambiguationData":[OSD([sQuery(id+"F2.wireOp",EDGE,"E18.1"),sQuery(id+"F2.wireOp",EDGE,"E35")])]})});
            var Q12;
            Q12=makeQuery(id+"F6.boolean.opBoolean","COPY",EDGE,{"derivedFrom":makeQuery(id+"F6.opExtrude","SWEPT_EDGE",EDGE,{"disambiguationData":[OSD([sQuery(id+"F2.wireOp",EDGE,"E18.3"),sQuery(id+"F2.wireOp",EDGE,"E30")])]})});
            var Q13;
            Q13=makeQuery(id+"F6.boolean.opBoolean","COPY",EDGE,{"derivedFrom":makeQuery(id+"F6.opExtrude","SWEPT_EDGE",EDGE,{"disambiguationData":[OSD([sQuery(id+"F2.wireOp",EDGE,"E17.4"),sQuery(id+"F2.wireOp",EDGE,"E30")])]})});
            var Q14;
            Q14=makeQuery(id+"F6.boolean.opBoolean","COPY",EDGE,{"derivedFrom":makeQuery(id+"F6.opExtrude","SWEPT_EDGE",EDGE,{"disambiguationData":[OSD([sQuery(id+"F2.wireOp",EDGE,"E17.2"),sQuery(id+"F2.wireOp",EDGE,"E17.4")])]})});
            var Q15;
            Q15=makeQuery(id+"F6.boolean.opBoolean","COPY",EDGE,{"derivedFrom":makeQuery(id+"F6.opExtrude","SWEPT_EDGE",EDGE,{"disambiguationData":[OSD([sQuery(id+"F2.wireOp",EDGE,"E17.1"),sQuery(id+"F2.wireOp",EDGE,"E17.2")])]})});
            var Q16;
            Q16=makeQuery(id+"F6.boolean.opBoolean","COPY",EDGE,{"derivedFrom":makeQuery(id+"F6.opExtrude","SWEPT_EDGE",EDGE,{"disambiguationData":[OSD([sQuery(id+"F2.wireOp",EDGE,"E17.1"),sQuery(id+"F2.wireOp",EDGE,"E31")])]})});
            var Q17;
            Q17=makeQuery(id+"F6.boolean.opBoolean","COPY",EDGE,{"derivedFrom":makeQuery(id+"F6.opExtrude","SWEPT_EDGE",EDGE,{"disambiguationData":[OSD([sQuery(id+"F2.wireOp",EDGE,"E18.1"),sQuery(id+"F2.wireOp",EDGE,"E31")])]})});
            var Q18;
            Q18=makeQuery(id+"F6.boolean.opBoolean","COPY",EDGE,{"derivedFrom":makeQuery(id+"F6.opExtrude","CAP_EDGE",EDGE,{"disambiguationData":[OSD([sQuery(id+"F2.wireOp",EDGE,"E30")])],"isStart":false})});
            var Q19;
            {var subQ0=sQuery(id+"F2.wireOp",EDGE,"E18.3");Q19=makeQuery(id+"F6.boolean.opBoolean","COPY",EDGE,{"derivedFrom":makeQuery(id+"F6.opExtrude","CAP_EDGE",EDGE,{"disambiguationData":[OSD([subQ0]),TDD([makeQuery(id+"F2.imprint","IMPRINT",EDGE,{"disambiguationData":[TD([[makeQuery(id+"F2.imprint","INTERSECT",VERTEX,{"derivedFrom":[sQuery(id+"F2.wireOp",EDGE,"E18.0"),subQ0]}),1.0]])],"derivedFrom":subQ0})])],"isStart":false})});}
            var Q20;
            Q20=makeQuery(id+"F6.boolean.opBoolean","COPY",EDGE,{"derivedFrom":makeQuery(id+"F6.opExtrude","CAP_EDGE",EDGE,{"disambiguationData":[OSD([sQuery(id+"F2.wireOp",EDGE,"E17.4")])],"isStart":false})});
            var Q21;
            Q21=makeQuery(id+"F6.boolean.opBoolean","COPY",EDGE,{"derivedFrom":makeQuery(id+"F6.opExtrude","CAP_EDGE",EDGE,{"disambiguationData":[OSD([sQuery(id+"F2.wireOp",EDGE,"E31")])],"isStart":false})});
            var Q22;
            {var subQ0=sQuery(id+"F2.wireOp",EDGE,"E18.1");Q22=makeQuery(id+"F6.boolean.opBoolean","COPY",EDGE,{"derivedFrom":makeQuery(id+"F6.opExtrude","CAP_EDGE",EDGE,{"disambiguationData":[OSD([subQ0]),TDD([makeQuery(id+"F2.imprint","IMPRINT",EDGE,{"disambiguationData":[TD([[makeQuery(id+"F2.imprint","INTERSECT",VERTEX,{"derivedFrom":[sQuery(id+"F2.wireOp",EDGE,"E18.0"),subQ0]}),1.0]])],"derivedFrom":subQ0})])],"isStart":false})});}
            var Q23;
            Q23=makeQuery(id+"F6.boolean.opBoolean","COPY",EDGE,{"derivedFrom":makeQuery(id+"F6.opExtrude","CAP_EDGE",EDGE,{"disambiguationData":[OSD([sQuery(id+"F2.wireOp",EDGE,"E18.0")])],"isStart":false})});
            var Q24;
            Q24=makeQuery(id+"F6.boolean.opBoolean","COPY",EDGE,{"derivedFrom":makeQuery(id+"F6.opExtrude","CAP_EDGE",EDGE,{"disambiguationData":[OSD([sQuery(id+"F2.wireOp",EDGE,"E18.2")])],"isStart":false})});
            var Q25;
            {var subQ0=sQuery(id+"F2.wireOp",EDGE,"E18.1");Q25=makeQuery(id+"F6.boolean.opBoolean","COPY",EDGE,{"derivedFrom":makeQuery(id+"F6.opExtrude","CAP_EDGE",EDGE,{"disambiguationData":[OSD([subQ0]),TDD([makeQuery(id+"F2.imprint","IMPRINT",EDGE,{"disambiguationData":[TD([[makeQuery(id+"F2.imprint","INTERSECT",VERTEX,{"derivedFrom":[subQ0,sQuery(id+"F2.wireOp",EDGE,"E18.2")]}),-1.0]])],"derivedFrom":subQ0})])],"isStart":false})});}
            var Q26;
            {var subQ0=sQuery(id+"F2.wireOp",EDGE,"E18.3");Q26=makeQuery(id+"F6.boolean.opBoolean","COPY",EDGE,{"derivedFrom":makeQuery(id+"F6.opExtrude","CAP_EDGE",EDGE,{"disambiguationData":[OSD([subQ0]),TDD([makeQuery(id+"F2.imprint","IMPRINT",EDGE,{"disambiguationData":[TD([[makeQuery(id+"F2.imprint","INTERSECT",VERTEX,{"derivedFrom":[sQuery(id+"F2.wireOp",EDGE,"E18.2"),subQ0]}),-1.0]])],"derivedFrom":subQ0})])],"isStart":false})});}
            var Q27;
            Q27=makeQuery(id+"F6.boolean.opBoolean","COPY",EDGE,{"derivedFrom":makeQuery(id+"F6.opExtrude","CAP_EDGE",EDGE,{"disambiguationData":[OSD([sQuery(id+"F2.wireOp",EDGE,"E34")])],"isStart":false})});
            var Q28;
            Q28=makeQuery(id+"F6.boolean.opBoolean","COPY",EDGE,{"derivedFrom":makeQuery(id+"F6.opExtrude","CAP_EDGE",EDGE,{"disambiguationData":[OSD([sQuery(id+"F2.wireOp",EDGE,"EJ5IJOJ9-0Wg4-q7mS-SvvP-tDIpZY0HjwDq")])],"isStart":false})});
            var Q29;
            Q29=makeQuery(id+"F6.boolean.opBoolean","COPY",EDGE,{"derivedFrom":makeQuery(id+"F6.opExtrude","CAP_EDGE",EDGE,{"disambiguationData":[OSD([sQuery(id+"F2.wireOp",EDGE,"E35")])],"isStart":false})});
            var Q30;
            {var subQ0=sQuery(id+"F2.wireOp",EDGE,"E20");Q30=makeQuery(id+"F6.boolean.opBoolean","COPY",EDGE,{"derivedFrom":makeQuery(id+"F6.opExtrude","CAP_EDGE",EDGE,{"disambiguationData":[OSD([subQ0]),TDD([makeQuery(id+"F2.imprint","IMPRINT",EDGE,{"disambiguationData":[TD([[makeQuery(id+"F2.imprint","INTERSECT",VERTEX,{"derivedFrom":[sQuery(id+"F2.wireOp",EDGE,"E18.3"),subQ0]}),1.0]])],"derivedFrom":subQ0})])],"isStart":false})});}
            var Q31;
            {var subQ0=sQuery(id+"F2.wireOp",EDGE,"E18.3");Q31=makeQuery(id+"F6.boolean.opBoolean","COPY",EDGE,{"derivedFrom":makeQuery(id+"F6.opExtrude","CAP_EDGE",EDGE,{"disambiguationData":[OSD([subQ0]),TDD([makeQuery(id+"F2.imprint","IMPRINT",EDGE,{"disambiguationData":[TD([[makeQuery(id+"F2.imprint","INTERSECT",VERTEX,{"derivedFrom":[subQ0,sQuery(id+"F2.wireOp",EDGE,"E19")]}),1.0]])],"derivedFrom":subQ0})])],"isStart":false})});}
            var Q32;
            {var subQ0=sQuery(id+"F2.wireOp",EDGE,"E19");Q32=makeQuery(id+"F6.boolean.opBoolean","COPY",EDGE,{"derivedFrom":makeQuery(id+"F6.opExtrude","CAP_EDGE",EDGE,{"disambiguationData":[OSD([subQ0]),TDD([makeQuery(id+"F2.imprint","IMPRINT",EDGE,{"disambiguationData":[TD([[makeQuery(id+"F2.imprint","INTERSECT",VERTEX,{"derivedFrom":[sQuery(id+"F2.wireOp",EDGE,"E18.3"),subQ0]}),1.0]])],"derivedFrom":subQ0})])],"isStart":false})});}
            var Q33;
            Q33=makeQuery(id+"F6.boolean.opBoolean","COPY",EDGE,{"derivedFrom":makeQuery(id+"F6.opExtrude","CAP_EDGE",EDGE,{"disambiguationData":[OSD([sQuery(id+"F2.wireOp",EDGE,"FMWFYpV9-Ew7e-ZcVp-ZZrZ-oKRKmoRq2qlx")])],"isStart":false})});
            var Q34;
            Q34=makeQuery(id+"F6.boolean.opBoolean","COPY",EDGE,{"derivedFrom":makeQuery(id+"F6.opExtrude","CAP_EDGE",EDGE,{"disambiguationData":[OSD([sQuery(id+"F2.wireOp",EDGE,"72itZujO-k5kq-emlP-LSjC-fSTvy6e93rC8")])],"isStart":false})});
            var Q35;
            {var subQ0=sQuery(id+"F2.wireOp",EDGE,"E20");Q35=makeQuery(id+"F6.boolean.opBoolean","COPY",EDGE,{"derivedFrom":makeQuery(id+"F6.opExtrude","CAP_EDGE",EDGE,{"disambiguationData":[OSD([subQ0]),TDD([makeQuery(id+"F2.imprint","IMPRINT",EDGE,{"disambiguationData":[TD([[makeQuery(id+"F2.imprint","INTERSECT",VERTEX,{"derivedFrom":[subQ0,sQuery(id+"F2.wireOp",EDGE,"72itZujO-k5kq-emlP-LSjC-fSTvy6e93rC8")]}),1.0]])],"derivedFrom":subQ0})])],"isStart":false})});}
            var Q36;
            Q36=makeQuery(id+"F6.boolean.opBoolean","COPY",EDGE,{"derivedFrom":makeQuery(id+"F6.opExtrude","CAP_EDGE",EDGE,{"disambiguationData":[OSD([sQuery(id+"F2.wireOp",EDGE,"E33")])],"isStart":false})});
            var Q37;
            {var subQ0=sQuery(id+"F2.wireOp",EDGE,"E19");Q37=makeQuery(id+"F6.boolean.opBoolean","COPY",EDGE,{"derivedFrom":makeQuery(id+"F6.opExtrude","CAP_EDGE",EDGE,{"disambiguationData":[OSD([subQ0]),TDD([makeQuery(id+"F2.imprint","IMPRINT",EDGE,{"disambiguationData":[TD([[makeQuery(id+"F2.imprint","INTERSECT",VERTEX,{"derivedFrom":[subQ0,sQuery(id+"F2.wireOp",EDGE,"72itZujO-k5kq-emlP-LSjC-fSTvy6e93rC8")]}),1.0]])],"derivedFrom":subQ0})])],"isStart":false})});}
            var Q38;
            {var subQ0=sQuery(id+"F2.wireOp",EDGE,"E19");Q38=makeQuery(id+"F6.boolean.opBoolean","COPY",EDGE,{"derivedFrom":makeQuery(id+"F6.opExtrude","CAP_EDGE",EDGE,{"disambiguationData":[OSD([subQ0]),TDD([makeQuery(id+"F2.imprint","IMPRINT",EDGE,{"disambiguationData":[TD([[makeQuery(id+"F2.imprint","INTERSECT",VERTEX,{"derivedFrom":[subQ0,sQuery(id+"F2.wireOp",EDGE,"E21")]}),1.0]])],"derivedFrom":subQ0})])],"isStart":false})});}
            var Q39;
            {var subQ0=sQuery(id+"F2.wireOp",EDGE,"E27");Q39=makeQuery(id+"F6.boolean.opBoolean","COPY",EDGE,{"derivedFrom":makeQuery(id+"F6.opExtrude","CAP_EDGE",EDGE,{"disambiguationData":[OSD([subQ0]),TDD([makeQuery(id+"F2.imprint","IMPRINT",EDGE,{"disambiguationData":[TD([[makeQuery(id+"F2.imprint","INTERSECT",VERTEX,{"derivedFrom":[subQ0,sQuery(id+"F2.wireOp",EDGE,"E29")]}),1.0]])],"derivedFrom":subQ0})])],"isStart":false})});}
            var Q40;
            {var subQ0=sQuery(id+"F2.wireOp",EDGE,"E27");Q40=makeQuery(id+"F6.boolean.opBoolean","COPY",EDGE,{"derivedFrom":makeQuery(id+"F6.opExtrude","CAP_EDGE",EDGE,{"disambiguationData":[OSD([subQ0]),TDD([makeQuery(id+"F2.imprint","IMPRINT",EDGE,{"disambiguationData":[TD([[makeQuery(id+"F2.imprint","INTERSECT",VERTEX,{"derivedFrom":[subQ0,sQuery(id+"F2.wireOp",EDGE,"E32")]}),-1.0]])],"derivedFrom":subQ0})])],"isStart":false})});}
            var Q41;
            {var subQ0=sQuery(id+"F2.wireOp",EDGE,"E27");Q41=makeQuery(id+"F6.boolean.opBoolean","COPY",EDGE,{"derivedFrom":makeQuery(id+"F6.opExtrude","CAP_EDGE",EDGE,{"disambiguationData":[OSD([subQ0]),TDD([makeQuery(id+"F2.imprint","IMPRINT",EDGE,{"disambiguationData":[TD([[makeQuery(id+"F2.imprint","INTERSECT",VERTEX,{"derivedFrom":[sQuery(id+"F2.wireOp",EDGE,"E18.1"),subQ0]}),1.0]])],"derivedFrom":subQ0})])],"isStart":false})});}
            var Q42;
            {var subQ0=sQuery(id+"F2.wireOp",EDGE,"E20");Q42=makeQuery(id+"F6.boolean.opBoolean","COPY",EDGE,{"derivedFrom":makeQuery(id+"F6.opExtrude","CAP_EDGE",EDGE,{"disambiguationData":[OSD([subQ0]),TDD([makeQuery(id+"F2.imprint","IMPRINT",EDGE,{"disambiguationData":[TD([[makeQuery(id+"F2.imprint","INTERSECT",VERTEX,{"derivedFrom":[sQuery(id+"F2.wireOp",EDGE,"E17.5"),subQ0]}),-1.0]])],"derivedFrom":subQ0})])],"isStart":false})});}
            var Q43;
            {var subQ0=sQuery(id+"F2.wireOp",EDGE,"E28");Q43=makeQuery(id+"F6.boolean.opBoolean","COPY",EDGE,{"derivedFrom":makeQuery(id+"F6.opExtrude","CAP_EDGE",EDGE,{"disambiguationData":[OSD([subQ0]),TDD([makeQuery(id+"F2.imprint","IMPRINT",EDGE,{"disambiguationData":[TD([[makeQuery(id+"F2.imprint","INTERSECT",VERTEX,{"derivedFrom":[sQuery(id+"F2.wireOp",EDGE,"E17.3"),subQ0]}),-1.0]])],"derivedFrom":subQ0})])],"isStart":false})});}
            var Q44;
            {var subQ0=sQuery(id+"F2.wireOp",EDGE,"E28");Q44=makeQuery(id+"F6.boolean.opBoolean","COPY",EDGE,{"derivedFrom":makeQuery(id+"F6.opExtrude","CAP_EDGE",EDGE,{"disambiguationData":[OSD([subQ0]),TDD([makeQuery(id+"F2.imprint","IMPRINT",EDGE,{"disambiguationData":[TD([[makeQuery(id+"F2.imprint","INTERSECT",VERTEX,{"derivedFrom":[subQ0,sQuery(id+"F2.wireOp",EDGE,"E32")]}),-1.0]])],"derivedFrom":subQ0})])],"isStart":false})});}
            var Q45;
            {var subQ0=sQuery(id+"F2.wireOp",EDGE,"E28");Q45=makeQuery(id+"F6.boolean.opBoolean","COPY",EDGE,{"derivedFrom":makeQuery(id+"F6.opExtrude","CAP_EDGE",EDGE,{"disambiguationData":[OSD([subQ0]),TDD([makeQuery(id+"F2.imprint","IMPRINT",EDGE,{"disambiguationData":[TD([[makeQuery(id+"F2.imprint","INTERSECT",VERTEX,{"derivedFrom":[sQuery(id+"F2.wireOp",EDGE,"E18.1"),subQ0]}),1.0]])],"derivedFrom":subQ0})])],"isStart":false})});}
            var Q46;
            {var subQ0=sQuery(id+"F2.wireOp",EDGE,"E18.1");Q46=makeQuery(id+"F6.boolean.opBoolean","COPY",EDGE,{"derivedFrom":makeQuery(id+"F6.opExtrude","CAP_EDGE",EDGE,{"disambiguationData":[OSD([subQ0]),TDD([makeQuery(id+"F2.imprint","IMPRINT",EDGE,{"disambiguationData":[TD([[makeQuery(id+"F2.imprint","INTERSECT",VERTEX,{"derivedFrom":[subQ0,sQuery(id+"F2.wireOp",EDGE,"E27")]}),1.0]])],"derivedFrom":subQ0})])],"isStart":false})});}
            var Q47;
            Q47=makeQuery(id+"F6.boolean.opBoolean","COPY",EDGE,{"derivedFrom":makeQuery(id+"F6.opExtrude","CAP_EDGE",EDGE,{"disambiguationData":[OSD([sQuery(id+"F2.wireOp",EDGE,"oXTIdJ37-I2Sm-Fy2X-7b5Y-V1gPf1k4f7kg")])],"isStart":false})});
            var Q48;
            Q48=makeQuery(id+"F6.boolean.opBoolean","COPY",EDGE,{"derivedFrom":makeQuery(id+"F6.opExtrude","CAP_EDGE",EDGE,{"disambiguationData":[OSD([sQuery(id+"F2.wireOp",EDGE,"E29")])],"isStart":false})});
            var Q49;
            Q49=makeQuery(id+"F6.boolean.opBoolean","COPY",EDGE,{"derivedFrom":makeQuery(id+"F6.opExtrude","CAP_EDGE",EDGE,{"disambiguationData":[OSD([sQuery(id+"F2.wireOp",EDGE,"E17.5")])],"isStart":false})});
            var Q50;
            Q50=makeQuery(id+"F6.boolean.opBoolean","COPY",EDGE,{"derivedFrom":makeQuery(id+"F6.opExtrude","CAP_EDGE",EDGE,{"disambiguationData":[OSD([sQuery(id+"F2.wireOp",EDGE,"E21")])],"isStart":false})});
            var Q51;
            Q51=makeQuery(id+"F6.boolean.opBoolean","COPY",EDGE,{"derivedFrom":makeQuery(id+"F6.opExtrude","CAP_EDGE",EDGE,{"disambiguationData":[OSD([sQuery(id+"F2.wireOp",EDGE,"E17.3")])],"isStart":false})});
            var Q52;
            Q52=makeQuery(id+"F6.boolean.opBoolean","COPY",EDGE,{"derivedFrom":makeQuery(id+"F6.opExtrude","CAP_EDGE",EDGE,{"disambiguationData":[OSD([sQuery(id+"F2.wireOp",EDGE,"E32")])],"isStart":false})});
            var Q53;
            Q53=makeQuery(id+"F6.boolean.opBoolean","COPY",EDGE,{"derivedFrom":makeQuery(id+"F6.opExtrude","CAP_EDGE",EDGE,{"disambiguationData":[OSD([sQuery(id+"F2.wireOp",EDGE,"KB4tX4Ro-G294-vaRV-RxTP-gQnuyON8fFV4")])],"isStart":false})});
            var Q54;
            Q54=makeQuery(id+"F6.boolean.opBoolean","COPY",EDGE,{"derivedFrom":makeQuery(id+"F6.opExtrude","CAP_EDGE",EDGE,{"disambiguationData":[OSD([sQuery(id+"F2.wireOp",EDGE,"E17.0"),sQuery(id+"F2.wireOp",EDGE,"E22"),sQuery(id+"F2.wireOp",EDGE,"E26")])],"isStart":false})});
            var Q55;
            Q55=makeQuery(id+"F6.boolean.opBoolean","COPY",EDGE,{"derivedFrom":makeQuery(id+"F6.opExtrude","CAP_EDGE",EDGE,{"disambiguationData":[OSD([sQuery(id+"F2.wireOp",EDGE,"E23")])],"isStart":false})});
            var Q56;
            Q56=makeQuery(id+"F6.boolean.opBoolean","COPY",EDGE,{"derivedFrom":makeQuery(id+"F6.opExtrude","CAP_EDGE",EDGE,{"disambiguationData":[OSD([sQuery(id+"F2.wireOp",EDGE,"E24")])],"isStart":false})});
            var Q57;
            Q57=makeQuery(id+"F6.boolean.opBoolean","COPY",EDGE,{"derivedFrom":makeQuery(id+"F6.opExtrude","CAP_EDGE",EDGE,{"disambiguationData":[OSD([sQuery(id+"F2.wireOp",EDGE,"E25")])],"isStart":false})});
            var Q58;
            Q58=makeQuery(id+"F6.boolean.opBoolean","COPY",EDGE,{"derivedFrom":makeQuery(id+"F6.opExtrude","CAP_EDGE",EDGE,{"disambiguationData":[OSD([sQuery(id+"F2.wireOp",EDGE,"E38")])],"isStart":false})});
            var Q59;
            Q59=makeQuery(id+"F6.boolean.opBoolean","COPY",EDGE,{"derivedFrom":makeQuery(id+"F6.opExtrude","CAP_EDGE",EDGE,{"disambiguationData":[OSD([sQuery(id+"F2.wireOp",EDGE,"E14.0")])],"isStart":false})});
            var Q60;
            Q60=makeQuery(id+"F6.boolean.opBoolean","COPY",EDGE,{"derivedFrom":makeQuery(id+"F6.opExtrude","CAP_EDGE",EDGE,{"disambiguationData":[OSD([sQuery(id+"F2.wireOp",EDGE,"E15.0")])],"isStart":false})});
            var Q61;
            Q61=makeQuery(id+"F6.boolean.opBoolean","COPY",EDGE,{"derivedFrom":makeQuery(id+"F6.opExtrude","CAP_EDGE",EDGE,{"disambiguationData":[OSD([sQuery(id+"F2.wireOp",EDGE,"E40")])],"isStart":false})});
            var Q62;
            Q62=makeQuery(id+"F6.boolean.opBoolean","COPY",EDGE,{"derivedFrom":makeQuery(id+"F6.opExtrude","CAP_EDGE",EDGE,{"disambiguationData":[OSD([sQuery(id+"F2.wireOp",EDGE,"E43")])],"isStart":false})});
            var Q63;
            Q63=makeQuery(id+"F6.boolean.opBoolean","COPY",EDGE,{"derivedFrom":makeQuery(id+"F6.opExtrude","CAP_EDGE",EDGE,{"disambiguationData":[OSD([sQuery(id+"F2.wireOp",EDGE,"E42")])],"isStart":false})});
            var Q64;
            Q64=makeQuery(id+"F6.boolean.opBoolean","COPY",EDGE,{"derivedFrom":makeQuery(id+"F6.opExtrude","CAP_EDGE",EDGE,{"disambiguationData":[OSD([sQuery(id+"F2.wireOp",EDGE,"E44")])],"isStart":false})});
            fillet(context, id + "F10", {"entities" : qUnion([Q0, Q1, Q2, Q3, Q4, Q5, Q6, Q7, Q8, Q9, Q10, Q11, Q12, Q13, Q14, Q15, Q16, Q17, Q18, Q19, Q20, Q21, Q22, Q23, Q24, Q25, Q26, Q27, Q28, Q29, Q30, Q31, Q32, Q33, Q34, Q35, Q36, Q37, Q38, Q39, Q40, Q41, Q42, Q43, Q44, Q45, Q46, Q47, Q48, Q49, Q50, Q51, Q52, Q53, Q54, Q55, Q56, Q57, Q58, Q59, Q60, Q61, Q62, Q63, Q64]), "radius" : 2 * mm, "tangentPropagation" : true, "allowEdgeOverflow" : false});
        }
        {
            var Q0;
            Q0=makeQuery(id+"F8.opExtrude","SWEPT_EDGE",EDGE,{"disambiguationData":[OSD([sQuery(id+"F7.wireOp",EDGE,"E45.0"),sQuery(id+"F7.wireOp",EDGE,"E45.1")])]});
            var Q1;
            Q1=makeQuery(id+"F8.opExtrude","SWEPT_EDGE",EDGE,{"disambiguationData":[OSD([sQuery(id+"F7.wireOp",EDGE,"E45.1"),sQuery(id+"F7.wireOp",EDGE,"E45.2")])]});
            var Q2;
            Q2=makeQuery(id+"F8.opExtrude","SWEPT_EDGE",EDGE,{"disambiguationData":[OSD([sQuery(id+"F7.wireOp",EDGE,"E45.0"),sQuery(id+"F7.wireOp",EDGE,"E45.3")])]});
            var Q3;
            Q3=makeQuery(id+"F8.opExtrude","SWEPT_EDGE",EDGE,{"disambiguationData":[OSD([sQuery(id+"F7.wireOp",EDGE,"E45.2"),sQuery(id+"F7.wireOp",EDGE,"E45.3")])]});
            fillet(context, id + "F11", {"entities" : qUnion([Q0, Q1, Q2, Q3]), "radius" : 1 * mm, "tangentPropagation" : true, "allowEdgeOverflow" : false});
        }
    });
